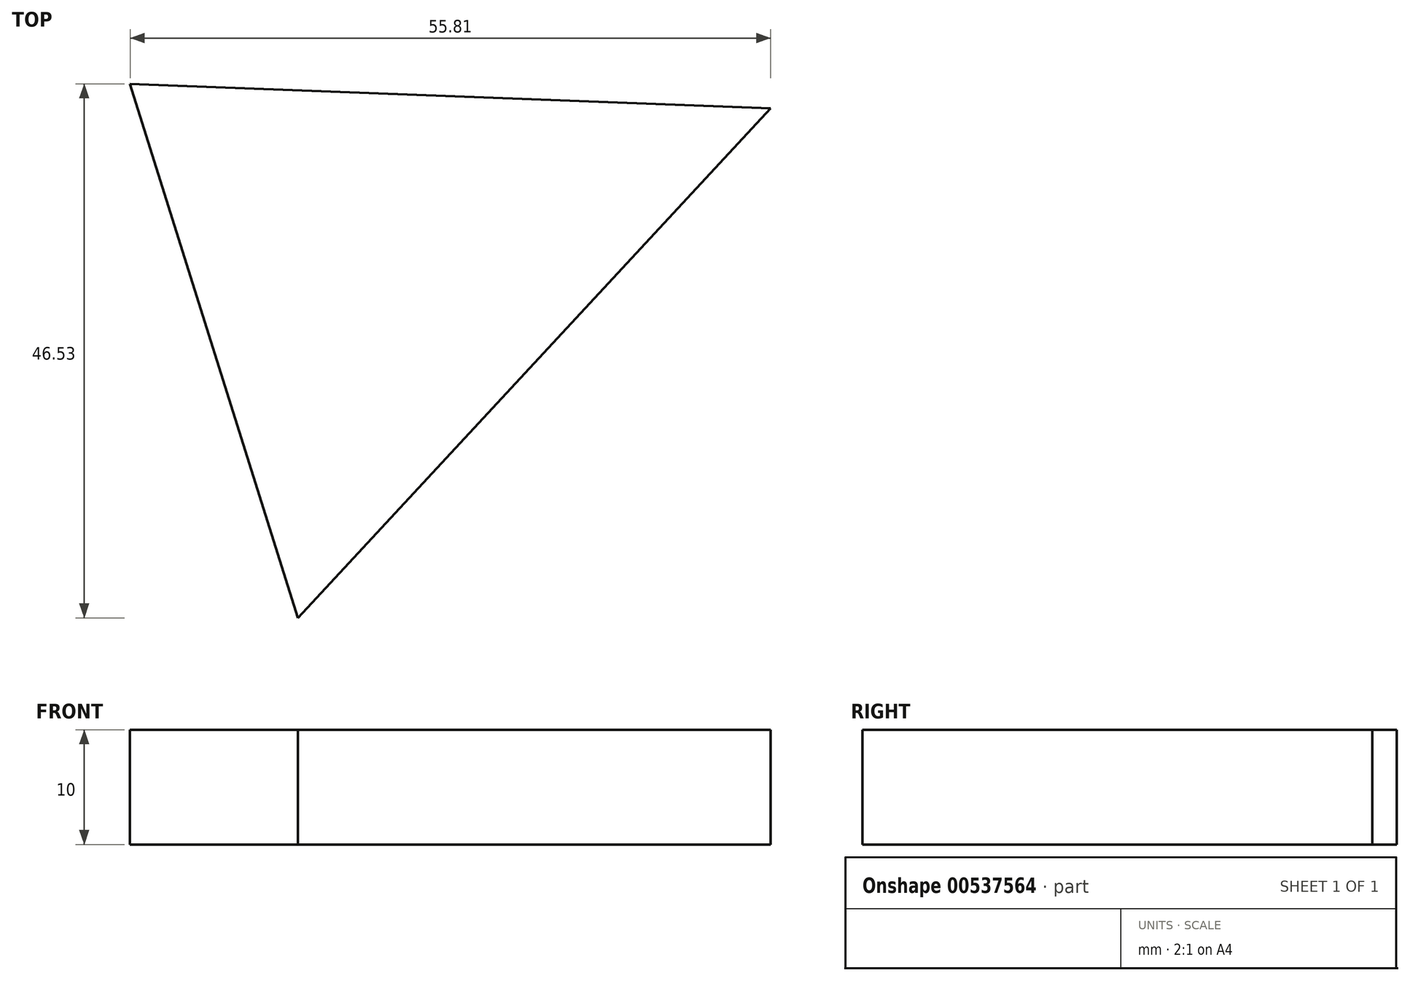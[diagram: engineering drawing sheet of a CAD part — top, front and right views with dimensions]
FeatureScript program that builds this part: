
annotation { "Feature Type Name" : "Feature", "Feature Type Description" : "" }
export const myFeature = defineFeature(function(context is Context, id is Id, definition is map)
    precondition{}
    {
        {
            var Q0;
            Q0=qCreatedBy(makeId("Top.planeOp"),FACE);
            var sketch = newSketch(context, id + "F0", { "sketchPlane" : qUnion([Q0])});
            skLineSegment(sketch, "E0", {"start": v(47.42, -25.37) * mm, "end": v(-8.4, -23.23) * mm});
            skLineSegment(sketch, "E1", {"start": v(47.42, -25.37) * mm, "end": v(6.23, -69.76) * mm});
            skLineSegment(sketch, "E2", {"start": v(6.23, -69.76) * mm, "end": v(-8.4, -23.23) * mm});
            skSolve(sketch);
        }
        {
            var Q0;
            Q0=makeQuery(id+"F0.imprint","IMPRINT",FACE,{"disambiguationData":[TD([[makeQuery(id+"F0.imprint","IMPRINT",EDGE,{"derivedFrom":sQuery(id+"F0.wireOp",EDGE,"E0")}),1.0]])]});
            extrude(context, id + "F1", {"entities" : qUnion([Q0]), "depth" : 10 * mm, "offsetDistance" : 25.4 * mm});
        }
    });
